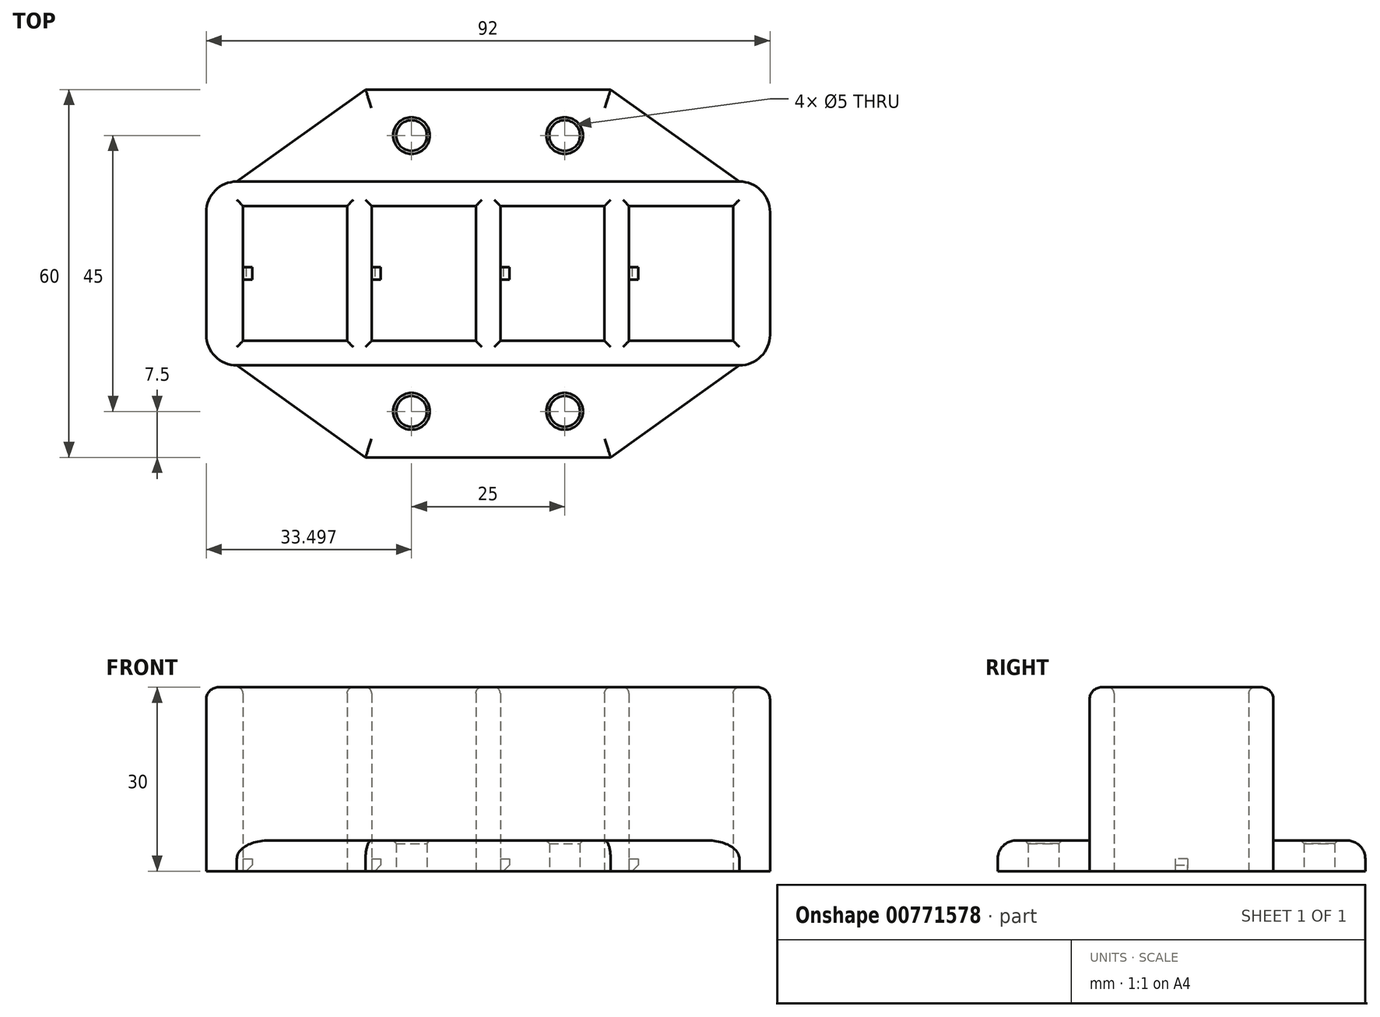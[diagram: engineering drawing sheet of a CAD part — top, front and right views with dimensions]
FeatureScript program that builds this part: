
annotation { "Feature Type Name" : "Feature", "Feature Type Description" : "" }
export const myFeature = defineFeature(function(context is Context, id is Id, definition is map)
    precondition{}
    {
        {
            var Q0;
            Q0=qCreatedBy(makeId("Top.planeOp"),FACE);
            var sketch = newSketch(context, id + "F0", { "sketchPlane" : qUnion([Q0])});
            skLineSegment(sketch, "E0.bottom", {"start": v(-58.26, 26) * mm, "end": v(-41.26, 26) * mm});
            skLineSegment(sketch, "E0.top", {"start": v(-58.26, 4) * mm, "end": v(-41.26, 4) * mm});
            skLineSegment(sketch, "E0.left", {"start": v(-58.26, 26) * mm, "end": v(-58.26, 4) * mm});
            skLineSegment(sketch, "E0.right", {"start": v(-41.26, 26) * mm, "end": v(-41.26, 4) * mm});
            skLineSegment(sketch, "E1.bottom", {"start": v(-37.26, 26) * mm, "end": v(-20.26, 26) * mm});
            skLineSegment(sketch, "E1.top", {"start": v(-37.26, 4) * mm, "end": v(-20.26, 4) * mm});
            skLineSegment(sketch, "E1.left", {"start": v(-37.26, 26) * mm, "end": v(-37.26, 4) * mm});
            skLineSegment(sketch, "E1.right", {"start": v(-20.26, 26) * mm, "end": v(-20.26, 4) * mm});
            skLineSegment(sketch, "E2.bottom", {"start": v(-16.26, 26) * mm, "end": v(0.74, 26) * mm});
            skLineSegment(sketch, "E2.top", {"start": v(-16.26, 4) * mm, "end": v(0.74, 4) * mm});
            skLineSegment(sketch, "E2.left", {"start": v(-16.26, 26) * mm, "end": v(-16.26, 4) * mm});
            skLineSegment(sketch, "E2.right", {"start": v(0.74, 26) * mm, "end": v(0.74, 4) * mm});
            skLineSegment(sketch, "E3.bottom", {"start": v(4.74, 26) * mm, "end": v(21.74, 26) * mm});
            skLineSegment(sketch, "E3.top", {"start": v(4.74, 4) * mm, "end": v(21.74, 4) * mm});
            skLineSegment(sketch, "E3.left", {"start": v(4.74, 26) * mm, "end": v(4.74, 4) * mm});
            skLineSegment(sketch, "E3.right", {"start": v(21.74, 26) * mm, "end": v(21.74, 4) * mm});
            skLineSegment(sketch, "E4.bottom", {"start": v(-64.26, 30) * mm, "end": v(27.74, 30) * mm});
            skLineSegment(sketch, "E4.top", {"start": v(-64.26, 0) * mm, "end": v(27.74, 0) * mm});
            skLineSegment(sketch, "E4.left", {"start": v(-64.26, 30) * mm, "end": v(-64.26, 0) * mm});
            skLineSegment(sketch, "E4.right", {"start": v(27.74, 30) * mm, "end": v(27.74, 0) * mm});
            skSolve(sketch);
        }
        {
            var Q0;
            Q0 = qSketchRegion(id + "F0", true);
            extrude(context, id + "F1", {"entities" : qUnion([Q0]), "depth" : 30 * mm, "offsetDistance" : 25 * mm});
        }
        {
            var Q0;
            Q0=makeQuery(id+"F1.opExtrude","SWEPT_EDGE",EDGE,{"disambiguationData":[OSD([sQuery(id+"F0.wireOp",EDGE,"E4.top"),sQuery(id+"F0.wireOp",EDGE,"E4.right")])]});
            var Q1;
            Q1=makeQuery(id+"F1.opExtrude","SWEPT_EDGE",EDGE,{"disambiguationData":[OSD([sQuery(id+"F0.wireOp",EDGE,"E4.bottom"),sQuery(id+"F0.wireOp",EDGE,"E4.right")])]});
            var Q2;
            Q2=makeQuery(id+"F1.opExtrude","SWEPT_EDGE",EDGE,{"disambiguationData":[OSD([sQuery(id+"F0.wireOp",EDGE,"E4.top"),sQuery(id+"F0.wireOp",EDGE,"E4.left")])]});
            var Q3;
            Q3=makeQuery(id+"F1.opExtrude","SWEPT_EDGE",EDGE,{"disambiguationData":[OSD([sQuery(id+"F0.wireOp",EDGE,"E4.bottom"),sQuery(id+"F0.wireOp",EDGE,"E4.left")])]});
            fillet(context, id + "F2", {"entities" : qUnion([Q0, Q1, Q2, Q3]), "radius" : 5 * mm, "tangentPropagation" : true, "allowEdgeOverflow" : false});
        }
        {
            var Q0;
            Q0=makeQuery(id+"F1.opExtrude","CAP_EDGE",EDGE,{"disambiguationData":[OSD([sQuery(id+"F0.wireOp",EDGE,"E4.top")])],"isStart":false});
            var Q1;
            Q1=makeQuery(id+"F1.opExtrude","CAP_EDGE",EDGE,{"disambiguationData":[OSD([sQuery(id+"F0.wireOp",EDGE,"E4.bottom")])],"isStart":false});
            fillet(context, id + "F3", {"entities" : qUnion([Q0, Q1]), "radius" : 2 * mm, "tangentPropagation" : true, "allowEdgeOverflow" : false});
        }
        {
            var Q0;
            Q0=makeQuery(id+"F1.opExtrude","CAP_EDGE",EDGE,{"disambiguationData":[OSD([sQuery(id+"F0.wireOp",EDGE,"E0.left")])],"isStart":false});
            var Q1;
            Q1=makeQuery(id+"F1.opExtrude","CAP_EDGE",EDGE,{"disambiguationData":[OSD([sQuery(id+"F0.wireOp",EDGE,"E0.top")])],"isStart":false});
            var Q2;
            Q2=makeQuery(id+"F1.opExtrude","CAP_EDGE",EDGE,{"disambiguationData":[OSD([sQuery(id+"F0.wireOp",EDGE,"E0.right")])],"isStart":false});
            var Q3;
            Q3=makeQuery(id+"F1.opExtrude","CAP_EDGE",EDGE,{"disambiguationData":[OSD([sQuery(id+"F0.wireOp",EDGE,"E0.bottom")])],"isStart":false});
            var Q4;
            Q4=makeQuery(id+"F1.opExtrude","CAP_EDGE",EDGE,{"disambiguationData":[OSD([sQuery(id+"F0.wireOp",EDGE,"E1.left")])],"isStart":false});
            var Q5;
            Q5=makeQuery(id+"F1.opExtrude","CAP_EDGE",EDGE,{"disambiguationData":[OSD([sQuery(id+"F0.wireOp",EDGE,"E1.bottom")])],"isStart":false});
            var Q6;
            Q6=makeQuery(id+"F1.opExtrude","CAP_EDGE",EDGE,{"disambiguationData":[OSD([sQuery(id+"F0.wireOp",EDGE,"E1.right")])],"isStart":false});
            var Q7;
            Q7=makeQuery(id+"F1.opExtrude","CAP_EDGE",EDGE,{"disambiguationData":[OSD([sQuery(id+"F0.wireOp",EDGE,"E1.top")])],"isStart":false});
            var Q8;
            Q8=makeQuery(id+"F1.opExtrude","CAP_EDGE",EDGE,{"disambiguationData":[OSD([sQuery(id+"F0.wireOp",EDGE,"E2.left")])],"isStart":false});
            var Q9;
            Q9=makeQuery(id+"F1.opExtrude","CAP_EDGE",EDGE,{"disambiguationData":[OSD([sQuery(id+"F0.wireOp",EDGE,"E2.bottom")])],"isStart":false});
            var Q10;
            Q10=makeQuery(id+"F1.opExtrude","CAP_EDGE",EDGE,{"disambiguationData":[OSD([sQuery(id+"F0.wireOp",EDGE,"E2.right")])],"isStart":false});
            var Q11;
            Q11=makeQuery(id+"F1.opExtrude","CAP_EDGE",EDGE,{"disambiguationData":[OSD([sQuery(id+"F0.wireOp",EDGE,"E2.top")])],"isStart":false});
            var Q12;
            Q12=makeQuery(id+"F1.opExtrude","CAP_EDGE",EDGE,{"disambiguationData":[OSD([sQuery(id+"F0.wireOp",EDGE,"E3.left")])],"isStart":false});
            var Q13;
            Q13=makeQuery(id+"F1.opExtrude","CAP_EDGE",EDGE,{"disambiguationData":[OSD([sQuery(id+"F0.wireOp",EDGE,"E3.bottom")])],"isStart":false});
            var Q14;
            Q14=makeQuery(id+"F1.opExtrude","CAP_EDGE",EDGE,{"disambiguationData":[OSD([sQuery(id+"F0.wireOp",EDGE,"E3.right")])],"isStart":false});
            var Q15;
            Q15=makeQuery(id+"F1.opExtrude","CAP_EDGE",EDGE,{"disambiguationData":[OSD([sQuery(id+"F0.wireOp",EDGE,"E3.top")])],"isStart":false});
            fillet(context, id + "F4", {"entities" : qUnion([Q0, Q1, Q2, Q3, Q4, Q5, Q6, Q7, Q8, Q9, Q10, Q11, Q12, Q13, Q14, Q15]), "radius" : 1 * mm, "tangentPropagation" : true, "allowEdgeOverflow" : false});
        }
        {
            var Q0;
            Q0=makeQuery(id+"F1.opExtrude","CAP_FACE",FACE,{"disambiguationData":[OSD([sQuery(id+"F0.wireOp",EDGE,"E0.bottom"),sQuery(id+"F0.wireOp",EDGE,"E0.top"),sQuery(id+"F0.wireOp",EDGE,"E0.left"),sQuery(id+"F0.wireOp",EDGE,"E0.right"),sQuery(id+"F0.wireOp",EDGE,"E1.bottom"),sQuery(id+"F0.wireOp",EDGE,"E1.top"),sQuery(id+"F0.wireOp",EDGE,"E1.left"),sQuery(id+"F0.wireOp",EDGE,"E1.right"),sQuery(id+"F0.wireOp",EDGE,"E2.bottom"),sQuery(id+"F0.wireOp",EDGE,"E2.top"),sQuery(id+"F0.wireOp",EDGE,"E2.left"),sQuery(id+"F0.wireOp",EDGE,"E2.right"),sQuery(id+"F0.wireOp",EDGE,"E3.bottom"),sQuery(id+"F0.wireOp",EDGE,"E3.top"),sQuery(id+"F0.wireOp",EDGE,"E3.left"),sQuery(id+"F0.wireOp",EDGE,"E3.right"),sQuery(id+"F0.wireOp",EDGE,"E4.bottom"),sQuery(id+"F0.wireOp",EDGE,"E4.top"),sQuery(id+"F0.wireOp",EDGE,"E4.left"),sQuery(id+"F0.wireOp",EDGE,"E4.right")])],"isStart":true});
            var sketch = newSketch(context, id + "F5", { "sketchPlane" : qUnion([Q0])});
            skLineSegment(sketch, "E5", {"start": v(-58.26, -4) * mm, "end": v(-58.26, -14) * mm});
            skLineSegment(sketch, "E6", {"start": v(-58.26, -14) * mm, "end": v(-56.76, -14) * mm});
            skLineSegment(sketch, "E7", {"start": v(-56.76, -14) * mm, "end": v(-56.76, -16) * mm});
            skLineSegment(sketch, "E8", {"start": v(-56.76, -16) * mm, "end": v(-58.26, -16) * mm});
            skLineSegment(sketch, "E9", {"start": v(-58.26, -16) * mm, "end": v(-58.26, -26) * mm});
            skLineSegment(sketch, "E10", {"start": v(-37.26, -4) * mm, "end": v(-37.26, -14) * mm});
            skLineSegment(sketch, "E11", {"start": v(-37.26, -14) * mm, "end": v(-35.76, -14) * mm});
            skLineSegment(sketch, "E12", {"start": v(-35.76, -14) * mm, "end": v(-35.76, -16) * mm});
            skLineSegment(sketch, "E13", {"start": v(-35.76, -16) * mm, "end": v(-37.26, -16) * mm});
            skLineSegment(sketch, "E14", {"start": v(-37.26, -16) * mm, "end": v(-37.26, -26) * mm});
            skLineSegment(sketch, "E15", {"start": v(-16.26, -4) * mm, "end": v(-16.26, -14) * mm});
            skLineSegment(sketch, "E16", {"start": v(-16.26, -14) * mm, "end": v(-14.76, -14) * mm});
            skLineSegment(sketch, "E17", {"start": v(-14.76, -14) * mm, "end": v(-14.76, -16) * mm});
            skLineSegment(sketch, "E18", {"start": v(-14.76, -16) * mm, "end": v(-16.26, -16) * mm});
            skLineSegment(sketch, "E19", {"start": v(-16.26, -16) * mm, "end": v(-16.26, -26) * mm});
            skLineSegment(sketch, "E20", {"start": v(4.74, -4) * mm, "end": v(4.74, -14) * mm});
            skLineSegment(sketch, "E21", {"start": v(4.74, -14) * mm, "end": v(6.24, -14) * mm});
            skLineSegment(sketch, "E22", {"start": v(6.24, -14) * mm, "end": v(6.24, -16) * mm});
            skLineSegment(sketch, "E23", {"start": v(6.24, -16) * mm, "end": v(4.74, -16) * mm});
            skLineSegment(sketch, "E24", {"start": v(4.74, -16) * mm, "end": v(4.74, -26) * mm});
            skLineSegment(sketch, "E25", {"start": v(-58.26, -16) * mm, "end": v(-58.26, -14) * mm});
            skLineSegment(sketch, "E26", {"start": v(-37.26, -16) * mm, "end": v(-37.26, -14) * mm});
            skLineSegment(sketch, "E27", {"start": v(-16.26, -16) * mm, "end": v(-16.26, -14) * mm});
            skLineSegment(sketch, "E28", {"start": v(4.74, -14) * mm, "end": v(4.74, -16) * mm});
            skSolve(sketch);
        }
        {
            var Q0;
            Q0 = qSketchRegion(id + "F5", true);
            extrude(context, id + "F6", {"entities" : qUnion([Q0]), "operationType" : NewBodyOperationType.ADD, "oppositeDirection" : true, "depth" : 2 * mm, "offsetDistance" : 25 * mm});
        }
        {
            var Q0;
            Q0=makeQuery(id+"F6.opExtrude","CAP_EDGE",EDGE,{"disambiguationData":[OSD([sQuery(id+"F5.wireOp",EDGE,"E7")])],"isStart":true});
            var Q1;
            Q1=makeQuery(id+"F6.opExtrude","CAP_EDGE",EDGE,{"disambiguationData":[OSD([sQuery(id+"F5.wireOp",EDGE,"E12")])],"isStart":true});
            var Q2;
            Q2=makeQuery(id+"F6.opExtrude","CAP_EDGE",EDGE,{"disambiguationData":[OSD([sQuery(id+"F5.wireOp",EDGE,"E17")])],"isStart":true});
            var Q3;
            Q3=makeQuery(id+"F6.opExtrude","CAP_EDGE",EDGE,{"disambiguationData":[OSD([sQuery(id+"F5.wireOp",EDGE,"E22")])],"isStart":true});
            chamfer(context, id + "F7", {"entities" : qUnion([Q0, Q1, Q2, Q3]), "width" : 1 * mm, "tangentPropagation" : true});
        }
        {
            var Q0;
            Q0=makeQuery(id+"F6.boolean.opBoolean","MERGE",FACE,{"derivedFrom":[makeQuery(id+"F1.opExtrude","CAP_FACE",FACE,{"disambiguationData":[OSD([sQuery(id+"F0.wireOp",EDGE,"E0.bottom"),sQuery(id+"F0.wireOp",EDGE,"E0.top"),sQuery(id+"F0.wireOp",EDGE,"E0.left"),sQuery(id+"F0.wireOp",EDGE,"E0.right"),sQuery(id+"F0.wireOp",EDGE,"E1.bottom"),sQuery(id+"F0.wireOp",EDGE,"E1.top"),sQuery(id+"F0.wireOp",EDGE,"E1.left"),sQuery(id+"F0.wireOp",EDGE,"E1.right"),sQuery(id+"F0.wireOp",EDGE,"E2.bottom"),sQuery(id+"F0.wireOp",EDGE,"E2.top"),sQuery(id+"F0.wireOp",EDGE,"E2.left"),sQuery(id+"F0.wireOp",EDGE,"E2.right"),sQuery(id+"F0.wireOp",EDGE,"E3.bottom"),sQuery(id+"F0.wireOp",EDGE,"E3.top"),sQuery(id+"F0.wireOp",EDGE,"E3.left"),sQuery(id+"F0.wireOp",EDGE,"E3.right"),sQuery(id+"F0.wireOp",EDGE,"E4.bottom"),sQuery(id+"F0.wireOp",EDGE,"E4.top"),sQuery(id+"F0.wireOp",EDGE,"E4.left"),sQuery(id+"F0.wireOp",EDGE,"E4.right")])],"isStart":true}),makeQuery(id+"F6.opExtrude","CAP_FACE",FACE,{"disambiguationData":[OSD([sQuery(id+"F5.wireOp",EDGE,"E6"),sQuery(id+"F5.wireOp",EDGE,"E7"),sQuery(id+"F5.wireOp",EDGE,"E8"),sQuery(id+"F5.wireOp",EDGE,"E25")])],"isStart":true}),makeQuery(id+"F6.opExtrude","CAP_FACE",FACE,{"disambiguationData":[OSD([sQuery(id+"F5.wireOp",EDGE,"E11"),sQuery(id+"F5.wireOp",EDGE,"E12"),sQuery(id+"F5.wireOp",EDGE,"E13"),sQuery(id+"F5.wireOp",EDGE,"E26")])],"isStart":true}),makeQuery(id+"F6.opExtrude","CAP_FACE",FACE,{"disambiguationData":[OSD([sQuery(id+"F5.wireOp",EDGE,"E16"),sQuery(id+"F5.wireOp",EDGE,"E17"),sQuery(id+"F5.wireOp",EDGE,"E18"),sQuery(id+"F5.wireOp",EDGE,"E27")])],"isStart":true}),makeQuery(id+"F6.opExtrude","CAP_FACE",FACE,{"disambiguationData":[OSD([sQuery(id+"F5.wireOp",EDGE,"E21"),sQuery(id+"F5.wireOp",EDGE,"E22"),sQuery(id+"F5.wireOp",EDGE,"E23"),sQuery(id+"F5.wireOp",EDGE,"E28")])],"isStart":true})]});
            var sketch = newSketch(context, id + "F8", { "sketchPlane" : qUnion([Q0])});
            skLineSegment(sketch, "E29.bottom", {"start": v(-38.26, 0) * mm, "end": v(1.74, 0) * mm});
            skLineSegment(sketch, "E29.top", {"start": v(-38.26, 15) * mm, "end": v(1.74, 15) * mm});
            skLineSegment(sketch, "E29.left", {"start": v(-38.26, 0) * mm, "end": v(-38.26, 15) * mm});
            skLineSegment(sketch, "E29.right", {"start": v(1.74, 0) * mm, "end": v(1.74, 15) * mm});
            skLineSegment(sketch, "E30", {"start": v(-38.26, 15) * mm, "end": v(-59.26, 0) * mm});
            skLineSegment(sketch, "E31", {"start": v(1.74, 15) * mm, "end": v(22.74, 0) * mm});
            skLineSegment(sketch, "E32.bottom", {"start": v(1.74, -30) * mm, "end": v(-38.26, -30) * mm});
            skLineSegment(sketch, "E32.top", {"start": v(1.74, -45) * mm, "end": v(-38.26, -45) * mm});
            skLineSegment(sketch, "E32.left", {"start": v(1.74, -30) * mm, "end": v(1.74, -45) * mm});
            skLineSegment(sketch, "E32.right", {"start": v(-38.26, -30) * mm, "end": v(-38.26, -45) * mm});
            skLineSegment(sketch, "E33", {"start": v(-59.26, -30) * mm, "end": v(-38.26, -45) * mm});
            skLineSegment(sketch, "E34", {"start": v(1.74, -45) * mm, "end": v(22.74, -30) * mm});
            skLineSegment(sketch, "E35", {"start": v(-59.26, 0) * mm, "end": v(-38.26, 0) * mm});
            skLineSegment(sketch, "E36", {"start": v(1.74, 0) * mm, "end": v(22.74, 0) * mm});
            skLineSegment(sketch, "E37", {"start": v(-59.26, -30) * mm, "end": v(-38.26, -30) * mm});
            skLineSegment(sketch, "E38", {"start": v(1.74, -30) * mm, "end": v(22.74, -30) * mm});
            skPoint(sketch, "E39", {"position": v(-30.76, -37.5) * mm});
            skPoint(sketch, "E40", {"position": v(-5.76, -37.5) * mm});
            skPoint(sketch, "E41", {"position": v(-5.76, 7.5) * mm});
            skPoint(sketch, "E42", {"position": v(-30.76, 7.5) * mm});
            skCircle(sketch, "E43", {"center": v(-5.76, -37.5) * mm, "radius": 2.5 * mm});
            skCircle(sketch, "E44", {"center": v(-30.76, -37.5) * mm, "radius": 2.5 * mm});
            skCircle(sketch, "E45", {"center": v(-30.76, 7.5) * mm, "radius": 2.5 * mm});
            skCircle(sketch, "E46", {"center": v(-5.76, 7.5) * mm, "radius": 2.5 * mm});
            skSolve(sketch);
        }
        {
            var Q0;
            Q0 = qSketchRegion(id + "F8", true);
            extrude(context, id + "F9", {"entities" : qUnion([Q0]), "operationType" : NewBodyOperationType.ADD, "oppositeDirection" : true, "depth" : 5 * mm, "offsetDistance" : 25 * mm});
        }
        {
            var Q0;
            Q0=makeQuery(id+"F9.opExtrude","CAP_EDGE",EDGE,{"disambiguationData":[OSD([sQuery(id+"F8.wireOp",EDGE,"E31")])],"isStart":false});
            var Q1;
            Q1=makeQuery(id+"F9.opExtrude","CAP_EDGE",EDGE,{"disambiguationData":[OSD([sQuery(id+"F8.wireOp",EDGE,"E29.top")])],"isStart":false});
            var Q2;
            Q2=makeQuery(id+"F9.opExtrude","CAP_EDGE",EDGE,{"disambiguationData":[OSD([sQuery(id+"F8.wireOp",EDGE,"E30")])],"isStart":false});
            var Q3;
            Q3=makeQuery(id+"F9.opExtrude","CAP_EDGE",EDGE,{"disambiguationData":[OSD([sQuery(id+"F8.wireOp",EDGE,"E34")])],"isStart":false});
            var Q4;
            Q4=makeQuery(id+"F9.opExtrude","CAP_EDGE",EDGE,{"disambiguationData":[OSD([sQuery(id+"F8.wireOp",EDGE,"E32.top")])],"isStart":false});
            var Q5;
            Q5=makeQuery(id+"F9.opExtrude","CAP_EDGE",EDGE,{"disambiguationData":[OSD([sQuery(id+"F8.wireOp",EDGE,"E33")])],"isStart":false});
            fillet(context, id + "F10", {"entities" : qUnion([Q0, Q1, Q2, Q3, Q4, Q5]), "radius" : 3 * mm, "tangentPropagation" : true, "allowEdgeOverflow" : false});
        }
        {
            var Q0;
            Q0=makeQuery(id+"F9.opExtrude","CAP_EDGE",EDGE,{"disambiguationData":[OSD([sQuery(id+"F8.wireOp",EDGE,"E43")])],"isStart":false});
            var Q1;
            Q1=makeQuery(id+"F9.opExtrude","CAP_EDGE",EDGE,{"disambiguationData":[OSD([sQuery(id+"F8.wireOp",EDGE,"E44")])],"isStart":false});
            var Q2;
            Q2=makeQuery(id+"F9.opExtrude","CAP_EDGE",EDGE,{"disambiguationData":[OSD([sQuery(id+"F8.wireOp",EDGE,"E46")])],"isStart":false});
            var Q3;
            Q3=makeQuery(id+"F9.opExtrude","CAP_EDGE",EDGE,{"disambiguationData":[OSD([sQuery(id+"F8.wireOp",EDGE,"E45")])],"isStart":false});
            chamfer(context, id + "F11", {"entities" : qUnion([Q0, Q1, Q2, Q3]), "width" : 0.5 * mm, "tangentPropagation" : true});
        }
    });
